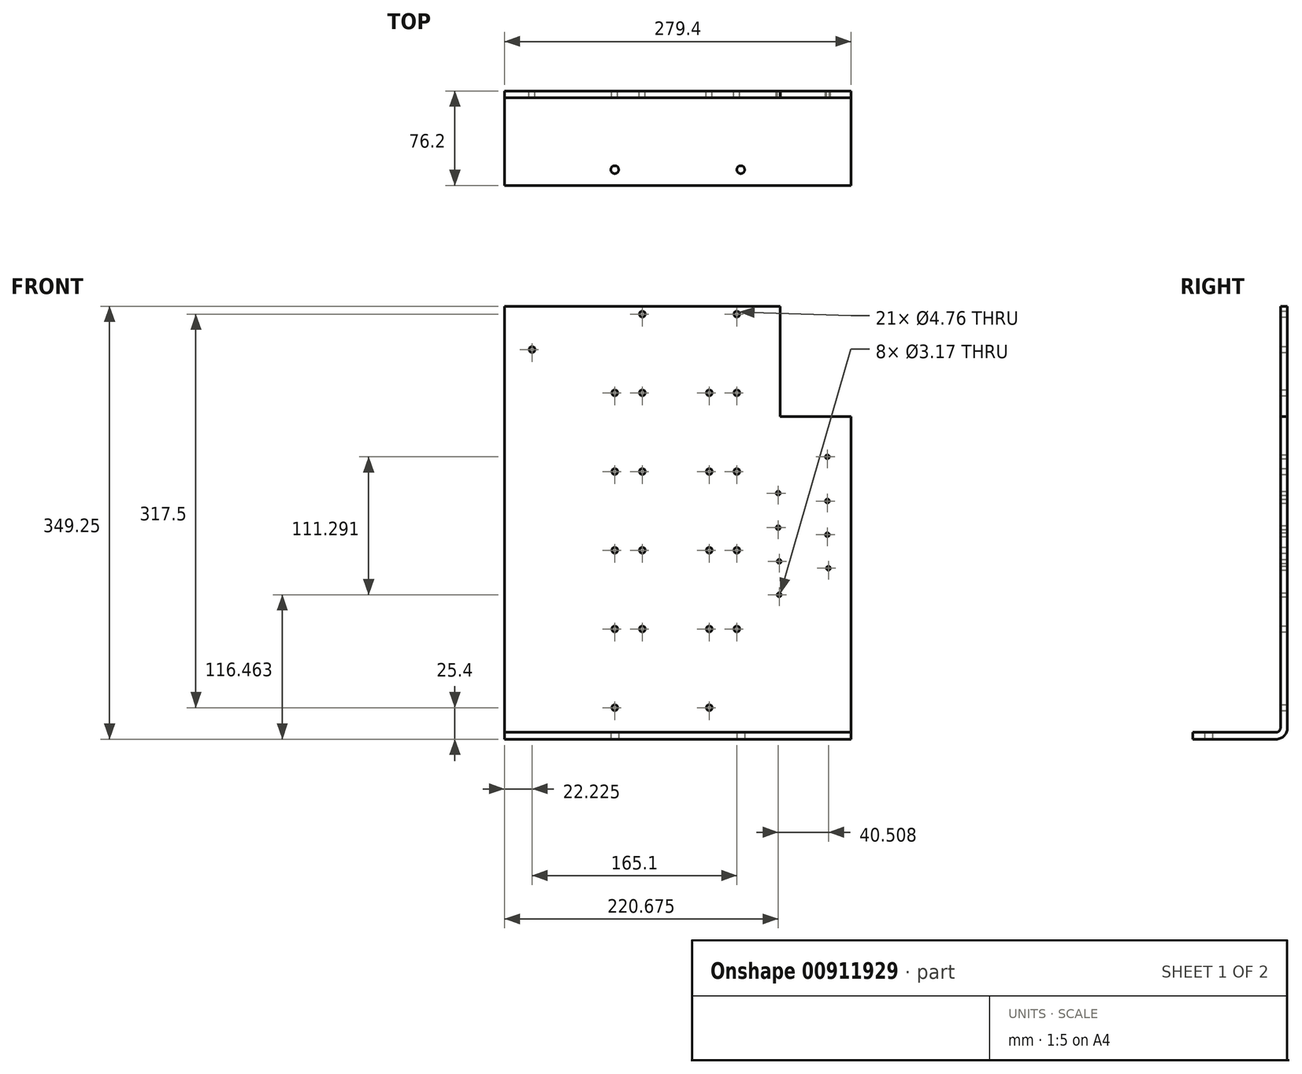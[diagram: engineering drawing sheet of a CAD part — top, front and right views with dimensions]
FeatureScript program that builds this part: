
annotation { "Feature Type Name" : "Feature", "Feature Type Description" : "" }
export const myFeature = defineFeature(function(context is Context, id is Id, definition is map)
    precondition{}
    {
        {
            var Q0;
            Q0=qCreatedBy(makeId("Right.planeOp"),FACE);
            var sketch = newSketch(context, id + "F0", { "sketchPlane" : qUnion([Q0])});
            skLineSegment(sketch, "E0", {"start": v(0, 0) * mm, "end": v(0, 5.56) * mm});
            skLineSegment(sketch, "E1", {"start": v(0, 0) * mm, "end": v(67.07, 0) * mm});
            skLineSegment(sketch, "E2", {"start": v(76.2, 9.13) * mm, "end": v(76.2, 349.25) * mm});
            skLineSegment(sketch, "E3", {"start": v(76.2, 349.25) * mm, "end": v(70.64, 349.25) * mm});
            skLineSegment(sketch, "E4", {"start": v(70.64, 349.25) * mm, "end": v(70.64, 9.13) * mm});
            skLineSegment(sketch, "E5", {"start": v(67.07, 5.56) * mm, "end": v(0, 5.56) * mm});
            skPoint(sketch, "E6.visualSharp", {"position": v(73.42, 2.78) * mm});
            skArc(sketch, "E7.0", {"start": v(67.07, 0) * mm, "mid": v(73.53, 2.67) * mm, "end": v(76.2, 9.13) * mm});
            skArc(sketch, "E8.0", {"start": v(67.07, 5.56) * mm, "mid": v(69.6, 6.6) * mm, "end": v(70.64, 9.13) * mm});
            skPoint(sketch, "E9.orphan", {"position": v(70.64, 5.56) * mm});
            skPoint(sketch, "E10.start.orphan", {"position": v(73.42, 349.25) * mm});
            skPoint(sketch, "E11.start.orphan", {"position": v(0, 2.78) * mm});
            skSolve(sketch);
        }
        {
            var Q0;
            Q0=makeQuery(id+"F0.imprint","IMPRINT",FACE,{"disambiguationData":[TD([[makeQuery(id+"F0.imprint","IMPRINT",EDGE,{"derivedFrom":sQuery(id+"F0.wireOp",EDGE,"E0")}),-1.0]])]});
            extrude(context, id + "F1", {"entities" : qUnion([Q0]), "depth" : 279.4 * mm, "offsetDistance" : 25.4 * mm});
        }
        {
            var Q0;
            Q0=makeQuery(id+"F1.opExtrude","SWEPT_FACE",FACE,{"disambiguationData":[OSD([sQuery(id+"F0.wireOp",EDGE,"E4")])]});
            var sketch = newSketch(context, id + "F2", { "sketchPlane" : qUnion([Q0])});
            skLineSegment(sketch, "E12", {"start": v(222.25, 349.25) * mm, "end": v(222.25, 260.35) * mm});
            skLineSegment(sketch, "E13", {"start": v(222.25, 260.35) * mm, "end": v(279.4, 260.35) * mm});
            skSolve(sketch);
        }
        {
            var Q0;
            {var subQ0=sQuery(id+"F2.wireOp",EDGE,"E12");Q0=makeQuery(id+"F2.imprint","IMPRINT",FACE,{"disambiguationData":[TD([[makeQuery(id+"F2.imprint","IMPRINT",EDGE,{"derivedFrom":subQ0}),1.0]])]});}
            extrude(context, id + "F3", {"entities" : qUnion([Q0]), "operationType" : NewBodyOperationType.REMOVE, "endBound" : BoundingType.THROUGH_ALL, "oppositeDirection" : true, "depth" : 25.4 * mm, "offsetDistance" : 25.4 * mm});
        }
        {
            var Q0;
            Q0=makeQuery(id+"F1.opExtrude","SWEPT_FACE",FACE,{"disambiguationData":[OSD([sQuery(id+"F0.wireOp",EDGE,"E2")])]});
            var sketch = newSketch(context, id + "F4", { "sketchPlane" : qUnion([Q0])});
            skPoint(sketch, "E14", {"position": v(-165.1, 279.4) * mm});
            skPoint(sketch, "E15", {"position": v(-111.12, 279.4) * mm});
            skPoint(sketch, "E16", {"position": v(-111.12, 215.9) * mm});
            skPoint(sketch, "E17", {"position": v(-165.1, 215.9) * mm});
            skPoint(sketch, "E18", {"position": v(-165.1, 152.4) * mm});
            skPoint(sketch, "E19", {"position": v(-111.12, 152.4) * mm});
            skPoint(sketch, "E20", {"position": v(-111.12, 88.9) * mm});
            skPoint(sketch, "E21", {"position": v(-165.1, 88.9) * mm});
            skPoint(sketch, "E22", {"position": v(-22.23, 314.33) * mm});
            skPoint(sketch, "E23", {"position": v(-187.33, 342.9) * mm});
            skPoint(sketch, "E24", {"position": v(-111.13, 342.9) * mm});
            skPoint(sketch, "E25", {"position": v(-88.9, 279.4) * mm});
            skPoint(sketch, "E26", {"position": v(-88.9, 215.9) * mm});
            skPoint(sketch, "E27", {"position": v(-88.9, 152.4) * mm});
            skPoint(sketch, "E28", {"position": v(-88.9, 88.9) * mm});
            skPoint(sketch, "E29", {"position": v(-88.9, 25.4) * mm});
            skPoint(sketch, "E30", {"position": v(-165.1, 25.4) * mm});
            skPoint(sketch, "E31", {"position": v(-187.33, 88.9) * mm});
            skPoint(sketch, "E32", {"position": v(-187.33, 152.4) * mm});
            skPoint(sketch, "E33", {"position": v(-187.33, 215.9) * mm});
            skPoint(sketch, "E34", {"position": v(-187.33, 279.4) * mm});
            skSolve(sketch);
        }
        {
            var Q0;
            Q0=makeQuery(id+"F1.opExtrude","SWEPT_FACE",FACE,{"disambiguationData":[OSD([sQuery(id+"F0.wireOp",EDGE,"E2")])]});
            var sketch = newSketch(context, id + "F5", { "sketchPlane" : qUnion([Q0])});
            skPoint(sketch, "E35", {"position": v(-260.35, 227.75) * mm});
            skPoint(sketch, "E36", {"position": v(-220.68, 198.44) * mm});
            skPoint(sketch, "E37", {"position": v(-260.35, 192.1) * mm});
            skPoint(sketch, "E38", {"position": v(-220.68, 170.66) * mm});
            skPoint(sketch, "E39", {"position": v(-260.35, 164.93) * mm});
            skPoint(sketch, "E40", {"position": v(-221.5, 143.49) * mm});
            skPoint(sketch, "E41", {"position": v(-261.18, 137.9) * mm});
            skPoint(sketch, "E42", {"position": v(-221.5, 116.46) * mm});
            skSolve(sketch);
        }
        {
            var Q0;
            Q0=sQuery(id+"F4.wireOp",VERTEX,"E23");
            var Q1;
            Q1=sQuery(id+"F4.wireOp",VERTEX,"E34");
            var Q2;
            Q2=sQuery(id+"F4.wireOp",VERTEX,"E33");
            var Q3;
            Q3=sQuery(id+"F4.wireOp",VERTEX,"E32");
            var Q4;
            Q4=sQuery(id+"F4.wireOp",VERTEX,"E31");
            var Q5;
            Q5=sQuery(id+"F4.wireOp",VERTEX,"E30");
            var Q6;
            Q6=sQuery(id+"F4.wireOp",VERTEX,"E21");
            var Q7;
            Q7=sQuery(id+"F4.wireOp",VERTEX,"E18");
            var Q8;
            Q8=sQuery(id+"F4.wireOp",VERTEX,"E17");
            var Q9;
            Q9=sQuery(id+"F4.wireOp",VERTEX,"E14");
            var Q10;
            Q10=sQuery(id+"F4.wireOp",VERTEX,"E24");
            var Q11;
            Q11=sQuery(id+"F4.wireOp",VERTEX,"E15");
            var Q12;
            Q12=sQuery(id+"F4.wireOp",VERTEX,"E16");
            var Q13;
            Q13=sQuery(id+"F4.wireOp",VERTEX,"E19");
            var Q14;
            Q14=sQuery(id+"F4.wireOp",VERTEX,"E20");
            var Q15;
            Q15=sQuery(id+"F4.wireOp",VERTEX,"E29");
            var Q16;
            Q16=sQuery(id+"F4.wireOp",VERTEX,"E28");
            var Q17;
            Q17=sQuery(id+"F4.wireOp",VERTEX,"E27");
            var Q18;
            Q18=sQuery(id+"F4.wireOp",VERTEX,"E26");
            var Q19;
            Q19=sQuery(id+"F4.wireOp",VERTEX,"E25");
            var Q20;
            Q20=sQuery(id+"F4.wireOp",VERTEX,"E22");
            var Q21;
            Q21=makeQuery(id+"F1.opExtrude","SWEPT_BODY",BODY,{"disambiguationData":[OSD([sQuery(id+"F0.wireOp",EDGE,"E0"),sQuery(id+"F0.wireOp",EDGE,"E1"),sQuery(id+"F0.wireOp",EDGE,"E2"),sQuery(id+"F0.wireOp",EDGE,"E3"),sQuery(id+"F0.wireOp",EDGE,"E4"),sQuery(id+"F0.wireOp",EDGE,"E5"),sQuery(id+"F0.wireOp",EDGE,"E7.0"),sQuery(id+"F0.wireOp",EDGE,"E8.0")])]});
            hole(context, id + "F6", {"style" : HoleStyle.SIMPLE, "endStyle" : HoleEndStyle.THROUGH, "holeDiameter" : 4.76 * mm, "majorDiameter" : 6.35 * mm, "isTappedThrough" : true, "tappedDepth" : 12.7 * mm, "tapClearance" : 3, "locations" : qUnion([Q0, Q1, Q2, Q3, Q4, Q5, Q6, Q7, Q8, Q9, Q10, Q11, Q12, Q13, Q14, Q15, Q16, Q17, Q18, Q19, Q20]), "scope" : qUnion([Q21])});
        }
        {
            var Q0;
            Q0=sQuery(id+"F5.wireOp",VERTEX,"E41");
            var Q1;
            Q1=sQuery(id+"F5.wireOp",VERTEX,"E42");
            var Q2;
            Q2=sQuery(id+"F5.wireOp",VERTEX,"E40");
            var Q3;
            Q3=sQuery(id+"F5.wireOp",VERTEX,"E39");
            var Q4;
            Q4=sQuery(id+"F5.wireOp",VERTEX,"E37");
            var Q5;
            Q5=sQuery(id+"F5.wireOp",VERTEX,"E38");
            var Q6;
            Q6=sQuery(id+"F5.wireOp",VERTEX,"E36");
            var Q7;
            Q7=sQuery(id+"F5.wireOp",VERTEX,"E35");
            var Q8;
            Q8=makeQuery(id+"F1.opExtrude","SWEPT_BODY",BODY,{"disambiguationData":[OSD([sQuery(id+"F0.wireOp",EDGE,"E0"),sQuery(id+"F0.wireOp",EDGE,"E1"),sQuery(id+"F0.wireOp",EDGE,"E2"),sQuery(id+"F0.wireOp",EDGE,"E3"),sQuery(id+"F0.wireOp",EDGE,"E4"),sQuery(id+"F0.wireOp",EDGE,"E5"),sQuery(id+"F0.wireOp",EDGE,"E7.0"),sQuery(id+"F0.wireOp",EDGE,"E8.0")])]});
            hole(context, id + "F7", {"style" : HoleStyle.SIMPLE, "endStyle" : HoleEndStyle.THROUGH, "holeDiameter" : 3.17 * mm, "majorDiameter" : 6.35 * mm, "isTappedThrough" : true, "tappedDepth" : 12.7 * mm, "tapClearance" : 3, "locations" : qUnion([Q0, Q1, Q2, Q3, Q4, Q5, Q6, Q7]), "scope" : qUnion([Q8])});
        }
        {
            var Q0;
            Q0=makeQuery(id+"F1.opExtrude","SWEPT_FACE",FACE,{"disambiguationData":[OSD([sQuery(id+"F0.wireOp",EDGE,"E1")])]});
            var sketch = newSketch(context, id + "F8", { "sketchPlane" : qUnion([Q0])});
            skPoint(sketch, "E43", {"position": v(88.9, -12.7) * mm});
            skPoint(sketch, "E44", {"position": v(190.5, -12.7) * mm});
            skSolve(sketch);
        }
        {
            var Q0;
            Q0=sQuery(id+"F8.wireOp",VERTEX,"E43");
            var Q1;
            Q1=sQuery(id+"F8.wireOp",VERTEX,"E44");
            var Q2;
            Q2=makeQuery(id+"F1.opExtrude","SWEPT_BODY",BODY,{"disambiguationData":[OSD([sQuery(id+"F0.wireOp",EDGE,"E0"),sQuery(id+"F0.wireOp",EDGE,"E1"),sQuery(id+"F0.wireOp",EDGE,"E2"),sQuery(id+"F0.wireOp",EDGE,"E3"),sQuery(id+"F0.wireOp",EDGE,"E4"),sQuery(id+"F0.wireOp",EDGE,"E5"),sQuery(id+"F0.wireOp",EDGE,"E7.0"),sQuery(id+"F0.wireOp",EDGE,"E8.0")])]});
            hole(context, id + "F9", {"style" : HoleStyle.SIMPLE, "endStyle" : HoleEndStyle.THROUGH, "holeDiameter" : 6.35 * mm, "majorDiameter" : 6.35 * mm, "isTappedThrough" : true, "tappedDepth" : 12.7 * mm, "tapClearance" : 3, "locations" : qUnion([Q0, Q1]), "scope" : qUnion([Q2])});
        }
    });
